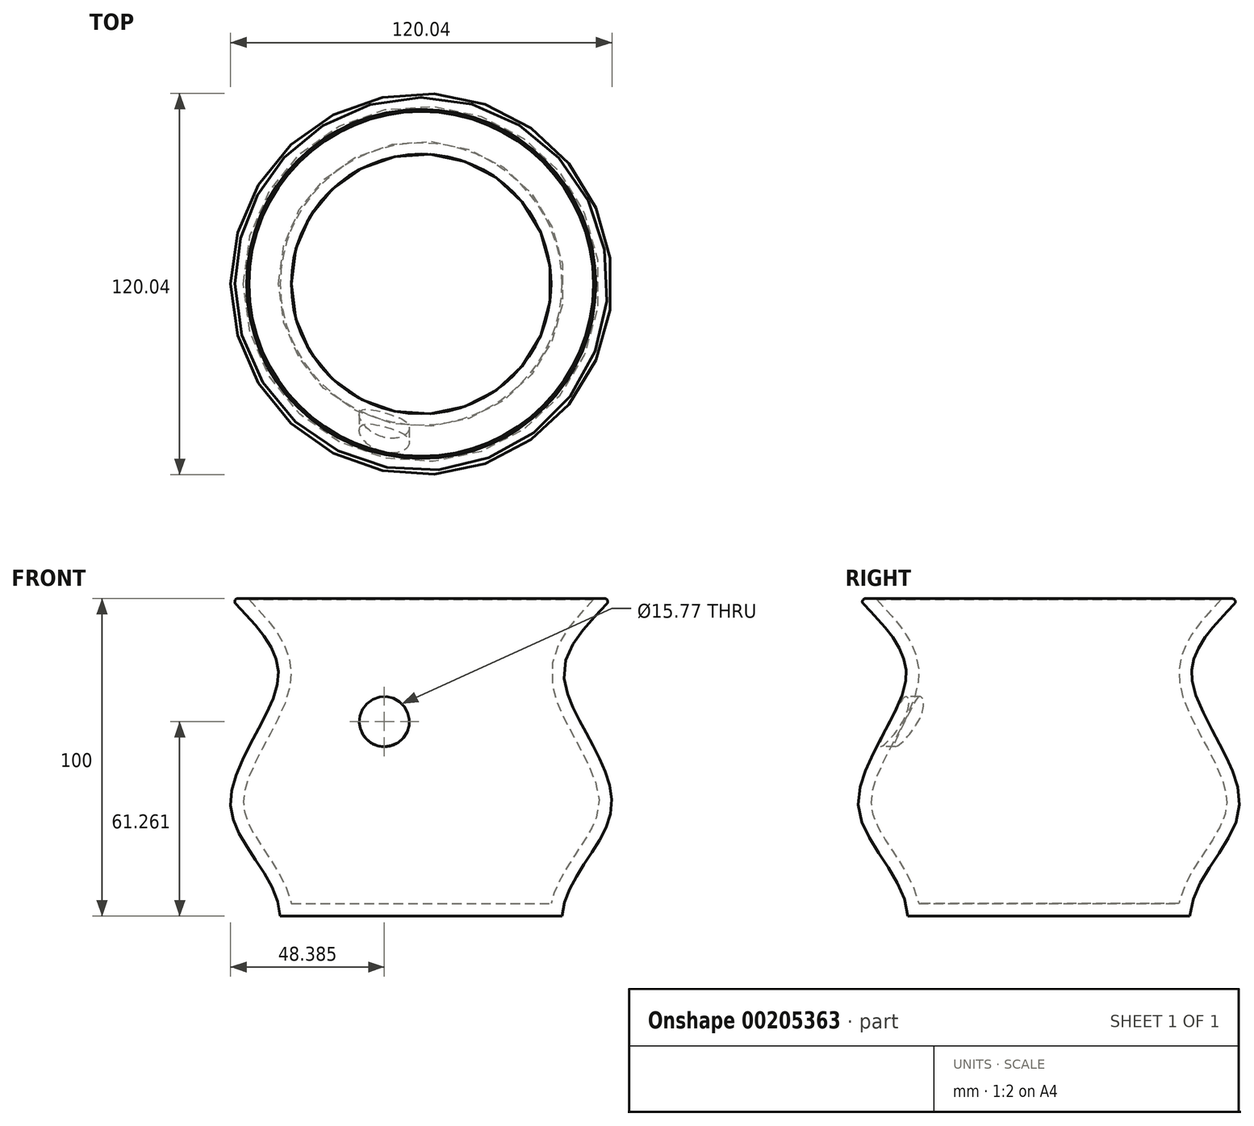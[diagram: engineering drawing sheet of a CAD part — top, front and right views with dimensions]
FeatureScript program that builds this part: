
annotation { "Feature Type Name" : "Feature", "Feature Type Description" : "" }
export const myFeature = defineFeature(function(context is Context, id is Id, definition is map)
    precondition{}
    {
        {
            var Q0;
            Q0=qCreatedBy(makeId("Front.planeOp"),FACE);
            var sketch = newSketch(context, id + "F0", { "sketchPlane" : qUnion([Q0])});
            skLineSegment(sketch, "E0.bottom", {"start": v(0, 0) * mm, "end": v(-44.38, 0) * mm});
            skLineSegment(sketch, "E0.top", {"start": v(0, 100) * mm, "end": v(-60, 100) * mm});
            skLineSegment(sketch, "E0.left", {"start": v(0, 0) * mm, "end": v(0, 100) * mm});
            skFitSpline(sketch, "E1", {"points": [v(-60, 100) * mm, v(-45, 75) * mm, v(-60, 35) * mm, v(-44.38, 0) * mm], "startDerivative": vector(73.98, -81.36) * mm, "endDerivative": vector(5.49, -112.73) * mm});
            skSolve(sketch);
        }
        {
            var Q0;
            Q0=makeQuery(id+"F0.imprint","IMPRINT",FACE,{"disambiguationData":[TD([[makeQuery(id+"F0.imprint","IMPRINT",EDGE,{"derivedFrom":sQuery(id+"F0.wireOp",EDGE,"E0.bottom")}),-1.0]])]});
            var Q1;
            Q1=sQuery(id+"F0.wireOp",EDGE,"E0.left");
            revolve(context, id + "F1", {"entities" : qUnion([Q0]), "axis" : qUnion([Q1]), "revolveType" : RevolveType.FULL});
        }
        {
            var Q0;
            Q0=makeQuery(id+"F1.opRevolve","SWEPT_FACE",FACE,{"disambiguationData":[OSD([sQuery(id+"F0.wireOp",EDGE,"E0.top")])]});
            shell(context, id + "F2", {"entities" : qUnion([Q0]), "thickness" : 4 * mm});
        }
        {
            var Q0;
            Q0=makeQuery(id+"F1.opRevolve","SWEPT_EDGE",EDGE,{"disambiguationData":[OSD([sQuery(id+"F0.wireOp",EDGE,"E0.top"),sQuery(id+"F0.wireOp",EDGE,"E1")])]});
            fillet(context, id + "F3", {"entities" : qUnion([Q0]), "radius" : 1 * mm, "tangentPropagation" : true, "allowEdgeOverflow" : false});
        }
        {
            var Q0;
            Q0=makeQuery(id+"F2.opShell","OFFSET_EDGE",EDGE,{"disambiguationData":[OSD([sQuery(id+"F0.wireOp",EDGE,"E0.top"),sQuery(id+"F0.wireOp",EDGE,"E1")])]});
            chamfer(context, id + "F4", {"entities" : qUnion([Q0]), "width" : 1 * mm, "tangentPropagation" : true});
        }
        {
            var Q0;
            Q0=qCreatedBy(makeId("Front.planeOp"),FACE);
            cPlane(context, id + "F5", {"entities" : qUnion([Q0]), "cplaneType" : CPlaneType.OFFSET, "offset" : 80 * mm, "width" : 150 * mm, "height" : 150 * mm});
        }
        {
            var Q0;
            Q0=qCreatedBy(id+"F5.planeOp",FACE);
            var sketch = newSketch(context, id + "F6", { "sketchPlane" : qUnion([Q0])});
            skCircle(sketch, "E2", {"center": v(-11.64, 61.26) * mm, "radius": 7.89 * mm});
            skSolve(sketch);
        }
        {
            var Q0;
            Q0=makeQuery(id+"F6.imprint","IMPRINT",FACE,{"disambiguationData":[TD([[makeQuery(id+"F6.imprint","IMPRINT",EDGE,{"derivedFrom":sQuery(id+"F6.wireOp",EDGE,"E2")}),1.0]])]});
            extrude(context, id + "F7", {"entities" : qUnion([Q0]), "operationType" : NewBodyOperationType.REMOVE, "oppositeDirection" : true, "depth" : 50 * mm});
        }
    });
